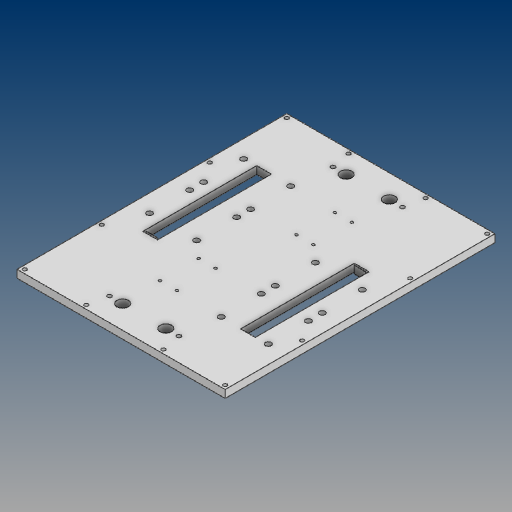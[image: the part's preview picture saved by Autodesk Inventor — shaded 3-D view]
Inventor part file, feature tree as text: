
AUTODESK INVENTOR PART (.ipt)
format: ipt  version: 2021 (Build 250183000, 183)  size: 283,136 bytes
history: native  units: mm
features: reference x32, other x13, sketch x6, hole x5, projected_geometry x3, extrude x2, mirror x2, pattern_circular x1
ambient origin geometry x8: Origin, YZ Plane, XZ Plane, XY Plane, X Axis, Y Axis, Z Axis, Center Point
bodies: Solid1 (feature_tree)
feature tree (64):
  extrude  "Extrusion1"  Depth=270.0mm
  hole  "Hole1"  [1 undecoded]
  mirror  "Mirror1"
  extrude  "Extrusion2"  Depth=100.0mm
  pattern_circular  "Circular Pattern1"  Count=10  [1 undecoded]
  sketch  "Sketch4"  dims[d8=80.0mm]
  hole  "Hole2"  [1 undecoded]
  hole  "Hole3"  [1 undecoded]
  hole  "Hole4"  [1 undecoded]
  hole  "Hole5"  [1 undecoded]
  mirror  "Mirror2"
  sketch  "Sketch1"  dims[d0=350.0mm d1=270.0mm]
  sketch  "Sketch2"  dims[d2=10.0mm d3=0.0mm d4=5.0mm]
  projected_geometry  "Projected Loop1"
  sketch  "Sketch3"  dims[d5=80.0mm d6=100.0mm d7=100.0mm]
  reference  "Reference1"
  reference  "Reference2"
  reference  "Reference3"
  reference  "Reference4"
  reference  "Reference5"
  reference  "Reference6"
  reference  "Reference7"
  reference  "Reference8"
  reference  "Reference9"
  reference  "Reference10"
  reference  "Reference11"
  reference  "Reference12"
  reference  "Reference13"
  reference  "Reference14"
  reference  "Reference15"
  reference  "Reference16"
  reference  "Reference17"
  reference  "Reference18"
  reference  "Reference19"
  reference  "Reference20"
  reference  "Reference21"
  reference  "Reference22"
  reference  "Reference23"
  reference  "Reference24"
  reference  "Reference25"
  reference  "Reference26"
  reference  "Reference27"
  reference  "Reference28"
  reference  "Reference29"
  reference  "Reference30"
  sketch  "Sketch5"  dims[d9=5.0mm d10=6.0mm d11=4.0mm d12=2.0mm d13=90.0deg d14=8.0mm d15=20.594885mm d16=0.0mm d17=0.0mm]
  projected_geometry  "Projected Loop2"
  sketch  "Sketch6"  dims[d18=2.0mm d19=20.0mm d20=360.0deg d22=0.5mm d23=0.5mm d24=7.5mm d25=6.0mm d26=4.0mm d27=2.0mm d28=90.0deg d29=8.0mm d30=20.594885mm d31=3.5mm d32=6.0mm d33=4.0mm d34=2.0mm d35=90.0deg d36=8.0mm d37=20.594885mm d38=56.0mm d39=30.0mm d40=15.0mm d41=6.0mm d42=4.0mm d43=2.0mm d44=90.0deg d45=8.0mm d46=20.594885mm d47=90.0mm d48=5.5mm d49=6.0mm d50=4.0mm d51=2.0mm d52=90.0deg d53=8.0mm d54=20.594885mm]
  projected_geometry  "Projected Loop3"
  reference  "Reference31"
  reference  "Reference32"
  other  "0001_ASS_Ban_lap_ghep_01.iam"
  other  "000ASS_Bo_banh_xe_04:1"
  other  "Spur Gear1:1"
  other  "Spur Gear2:1"
  other  "PK000:1"
  other  "PK000:2"
  other  "PK000:3"
  other  "PK000:4"
  other  "000ASS_Bo_banh_xe_04:2"
  other  "08_Ga_dong_co:1"
  other  "67060, ROLLER BALL BEARING:1"
  other  "67060, BODY, ROLLER BALL BEARING:1"
  other  "AS 1112 (2) - Metric M5  Type 5:2"
note: 6 required parameter values undecoded (feature->parameter linkage not recoverable at this tier; creation-order binding heuristic only, values carry confidence <= 0.55)
